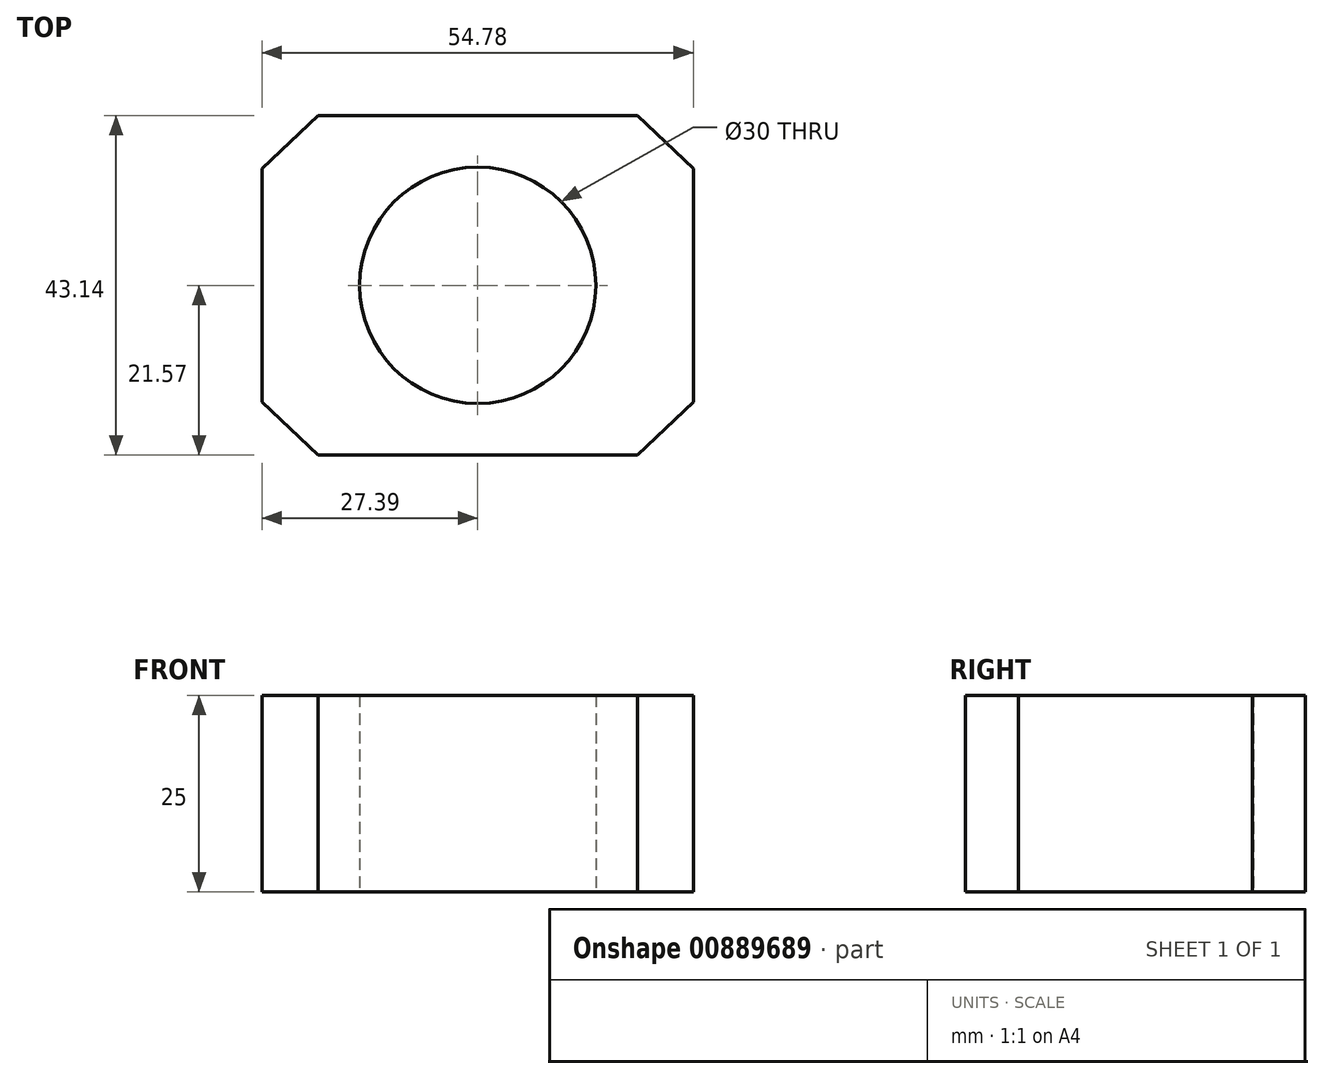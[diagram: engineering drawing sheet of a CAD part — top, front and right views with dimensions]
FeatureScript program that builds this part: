
annotation { "Feature Type Name" : "Feature", "Feature Type Description" : "" }
export const myFeature = defineFeature(function(context is Context, id is Id, definition is map)
    precondition{}
    {
        {
            var Q0;
            Q0=qCreatedBy(makeId("Top.planeOp"),FACE);
            var sketch = newSketch(context, id + "F0", { "sketchPlane" : qUnion([Q0])});
            skCircle(sketch, "E0", {"center": v(0, 0) * mm, "radius": 15 * mm});
            skLineSegment(sketch, "E1.bottom", {"start": v(20.3, -21.57) * mm, "end": v(-20.3, -21.57) * mm});
            skLineSegment(sketch, "E1.top", {"start": v(20.3, 21.57) * mm, "end": v(-20.3, 21.57) * mm});
            skLineSegment(sketch, "E1.left", {"start": v(27.39, -14.83) * mm, "end": v(27.39, 14.83) * mm});
            skLineSegment(sketch, "E1.right", {"start": v(-27.39, -14.83) * mm, "end": v(-27.39, 14.83) * mm});
            skLineSegment(sketch, "E2", {"start": v(-27.39, 14.83) * mm, "end": v(-20.3, 21.57) * mm});
            skPoint(sketch, "E3.orphan", {"position": v(-27.39, 21.57) * mm});
            skLineSegment(sketch, "E4.MirrorCS", {"start": v(-27.39, -14.83) * mm, "end": v(-20.3, -21.57) * mm});
            skPoint(sketch, "E5.orphan", {"position": v(-27.39, -21.57) * mm});
            skLineSegment(sketch, "E6.MirrorCS", {"start": v(27.39, 14.83) * mm, "end": v(20.3, 21.57) * mm});
            skLineSegment(sketch, "E7.MirrorCS", {"start": v(27.39, -14.83) * mm, "end": v(20.3, -21.57) * mm});
            skPoint(sketch, "E8.orphan", {"position": v(27.39, 21.57) * mm});
            skPoint(sketch, "E9.orphan", {"position": v(27.39, -21.57) * mm});
            skSolve(sketch);
        }
        {
            var Q0;
            Q0 = qSketchRegion(id + "F0", true);
            extrude(context, id + "F1", {"entities" : qUnion([Q0]), "depth" : 25 * mm, "offsetDistance" : 25 * mm});
        }
    });
